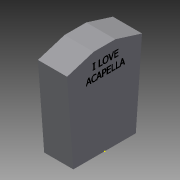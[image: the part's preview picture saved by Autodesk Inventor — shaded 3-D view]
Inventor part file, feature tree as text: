
AUTODESK INVENTOR PART (.ipt)
format: ipt  version: 2015 SP1 (Build 190203100, 203)  size: 80,384 bytes
history: native  units: in
note: dims shown in document units (in); Inventor stores cm internally (conversion verified against a paired STEP export)
features: sketch x3, extrude x1
ambient origin geometry x8: Origin, YZ Plane, XZ Plane, XY Plane, X Axis, Y Axis, Z Axis, Center Point
bodies: Solid1 (feature_tree)
feature tree (4):
  extrude  "Extrusion1"  Depth=6.7in
  sketch  "Sketch2"  dims[d6=15.0in]
  sketch  "Sketch3"  dims[d7=22.0in d8=20.0in d9=18.0in d10=7.0in d11=0.0in]
  sketch  "Sketch1"  dims[d4=6.7in d5=6.7in]
